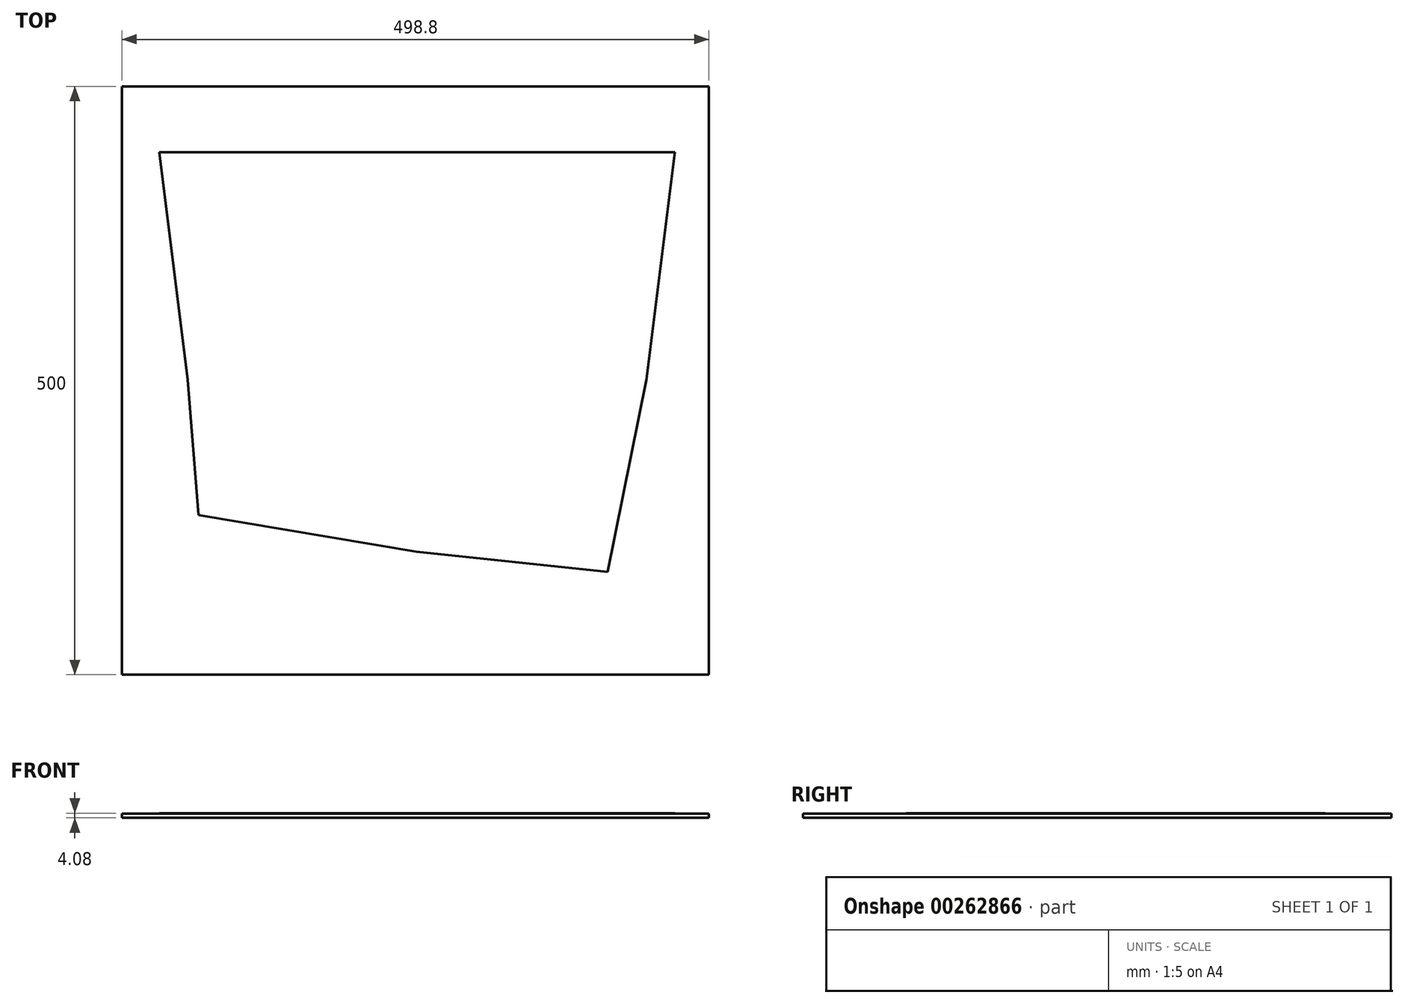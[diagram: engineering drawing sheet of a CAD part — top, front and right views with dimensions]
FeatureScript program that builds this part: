
annotation { "Feature Type Name" : "Feature", "Feature Type Description" : "" }
export const myFeature = defineFeature(function(context is Context, id is Id, definition is map)
    precondition{}
    {
        {
            var Q0;
            Q0=qCreatedBy(makeId("Top.planeOp"),FACE);
            var sketch = newSketch(context, id + "F0", { "sketchPlane" : qUnion([Q0])});
            skLineSegment(sketch, "E0.bottom", {"start": v(249.4, -250) * mm, "end": v(-249.4, -250) * mm});
            skLineSegment(sketch, "E0.top", {"start": v(249.4, 250) * mm, "end": v(-249.4, 250) * mm});
            skLineSegment(sketch, "E0.left", {"start": v(249.4, -250) * mm, "end": v(249.4, 250) * mm});
            skLineSegment(sketch, "E0.right", {"start": v(-249.4, -250) * mm, "end": v(-249.4, 250) * mm});
            skPoint(sketch, "E0.middle", {"position": v(0, 0) * mm});
            skSolve(sketch);
        }
        {
            var Q0;
            Q0=makeQuery(id+"F0.imprint","IMPRINT",FACE,{"disambiguationData":[TD([[makeQuery(id+"F0.imprint","IMPRINT",EDGE,{"derivedFrom":sQuery(id+"F0.wireOp",EDGE,"E0.bottom")}),-1.0]])]});
            extrude(context, id + "F5", {"entities" : qUnion([Q0]), "depth" : 3.58 * mm});
        }
        {
            var Q0;
            Q0=makeQuery(id+"F5.opExtrude","CAP_FACE",FACE,{"disambiguationData":[OSD([sQuery(id+"F0.wireOp",EDGE,"E0.bottom"),sQuery(id+"F0.wireOp",EDGE,"E0.top"),sQuery(id+"F0.wireOp",EDGE,"E0.left"),sQuery(id+"F0.wireOp",EDGE,"E0.right")])],"isStart":false});
            var sketch = newSketch(context, id + "F6", { "sketchPlane" : qUnion([Q0])});
            skSolve(sketch);
        }
        {
            var Q0;
            Q0=makeQuery(id+"F6.imprint","IMPRINT",FACE,{"disambiguationData":[TD([[makeQuery(id+"F6.imprint","IMPRINT",EDGE,{"derivedFrom":makeQuery(id+"F5.opExtrude","CAP_EDGE",EDGE,{"disambiguationData":[OSD([sQuery(id+"F0.wireOp",EDGE,"E0.bottom")])],"isStart":false})}),-1.0]])]});
            var sketch = newSketch(context, id + "F7", { "sketchPlane" : qUnion([Q0])});
            skLineSegment(sketch, "E1.0", {"start": v(249.4, 250) * mm, "end": v(-249.4, 250) * mm});
            skSolve(sketch);
        }
        {
            var Q0;
            Q0=makeQuery(id+"F6.imprint","IMPRINT",FACE,{"disambiguationData":[TD([[makeQuery(id+"F6.imprint","IMPRINT",EDGE,{"derivedFrom":makeQuery(id+"F5.opExtrude","CAP_EDGE",EDGE,{"disambiguationData":[OSD([sQuery(id+"F0.wireOp",EDGE,"E0.bottom")])],"isStart":false})}),-1.0]])]});
            var sketch = newSketch(context, id + "F1", { "sketchPlane" : qUnion([Q0])});
            skLineSegment(sketch, "E2", {"start": v(0, 0) * mm, "end": v(0, -288.47) * mm});
            skLineSegment(sketch, "E3", {"start": v(0, -288.47) * mm, "end": v(0, 364.66) * mm});
            skSolve(sketch);
        }
        {
            var Q0;
            Q0=makeQuery(id+"F7.imprint","IMPRINT",FACE,{"disambiguationData":[TD([[makeQuery(id+"F7.imprint","IMPRINT",EDGE,{"derivedFrom":sQuery(id+"F7.wireOp",EDGE,"E1.0")}),1.0]])]});
            var sketch = newSketch(context, id + "F2", { "sketchPlane" : qUnion([Q0])});
            skLineSegment(sketch, "E4", {"start": v(0, 0) * mm, "end": v(344.06, 0) * mm});
            skSolve(sketch);
        }
        {
            var Q0;
            Q0=makeQuery(id+"F7.imprint","IMPRINT",FACE,{"disambiguationData":[TD([[makeQuery(id+"F7.imprint","IMPRINT",EDGE,{"derivedFrom":sQuery(id+"F7.wireOp",EDGE,"E1.0")}),1.0]])]});
            var sketch = newSketch(context, id + "F8", { "sketchPlane" : qUnion([Q0])});
            skLineSegment(sketch, "E5", {"start": v(0, 0) * mm, "end": v(0, -150) * mm});
            skSolve(sketch);
        }
        {
            var Q0;
            Q0=makeQuery(id+"F8.imprint","IMPRINT",FACE,{"disambiguationData":[TD([[makeQuery(id+"F8.imprint","IMPRINT",EDGE,{"derivedFrom":makeQuery(id+"F7.imprint","IMPRINT",EDGE,{"derivedFrom":sQuery(id+"F7.wireOp",EDGE,"E1.0")})}),1.0]])]});
            var sketch = newSketch(context, id + "F9", { "sketchPlane" : qUnion([Q0])});
            skPoint(sketch, "E6", {"position": v(226.45, 198.2) * mm});
            skPoint(sketch, "E7", {"position": v(-226.46, 198.64) * mm});
            skPoint(sketch, "E8", {"position": v(-190.81, -119.49) * mm});
            skPoint(sketch, "E9", {"position": v(167.5, -166.98) * mm});
            skSolve(sketch);
        }
        {
            var Q0;
            Q0=makeQuery(id+"F8.imprint","IMPRINT",FACE,{"disambiguationData":[TD([[makeQuery(id+"F8.imprint","IMPRINT",EDGE,{"derivedFrom":makeQuery(id+"F7.imprint","IMPRINT",EDGE,{"derivedFrom":sQuery(id+"F7.wireOp",EDGE,"E1.0")})}),1.0]])]});
            var sketch = newSketch(context, id + "F3", { "sketchPlane" : qUnion([Q0])});
            skLineSegment(sketch, "E10", {"start": v(-224.62, 199.97) * mm, "end": v(0, 199.97) * mm});
            skLineSegment(sketch, "E11", {"start": v(0, 199.97) * mm, "end": v(227.13, 199.97) * mm});
            skLineSegment(sketch, "E12", {"start": v(202.14, 0) * mm, "end": v(167.97, -168.97) * mm});
            skLineSegment(sketch, "E13", {"start": v(167.97, -168.97) * mm, "end": v(0, -151.5) * mm});
            skLineSegment(sketch, "E14", {"start": v(0, -151.5) * mm, "end": v(-189.92, -119.5) * mm});
            skLineSegment(sketch, "E15", {"start": v(-189.92, -119.5) * mm, "end": v(-199.4, 0) * mm});
            skLineSegment(sketch, "E16", {"start": v(-199.4, 0) * mm, "end": v(-224.62, 199.97) * mm});
            skLineSegment(sketch, "E17", {"start": v(227.13, 199.97) * mm, "end": v(202.14, 0) * mm});
            skLineSegment(sketch, "E18", {"start": v(202.14, 0) * mm, "end": v(227.13, 199.97) * mm});
            skLineSegment(sketch, "E19", {"start": v(0, 199.97) * mm, "end": v(-224.62, 199.97) * mm});
            skLineSegment(sketch, "E20", {"start": v(-199.4, 0) * mm, "end": v(-189.92, -119.5) * mm});
            skLineSegment(sketch, "E21", {"start": v(0, -151.5) * mm, "end": v(167.97, -168.97) * mm});
            skSolve(sketch);
        }
        {
            var Q0;
            Q0=makeQuery(id+"F8.imprint","IMPRINT",FACE,{"disambiguationData":[TD([[makeQuery(id+"F8.imprint","IMPRINT",EDGE,{"derivedFrom":makeQuery(id+"F7.imprint","IMPRINT",EDGE,{"derivedFrom":sQuery(id+"F7.wireOp",EDGE,"E1.0")})}),1.0]])]});
            var sketch = newSketch(context, id + "F4", { "sketchPlane" : qUnion([Q0])});
            skLineSegment(sketch, "E22.0", {"start": v(0, 193.97) * mm, "end": v(-217.82, 193.97) * mm});
            skLineSegment(sketch, "E22.1", {"start": v(-193.43, 0.61) * mm, "end": v(-217.82, 193.97) * mm});
            skLineSegment(sketch, "E22.2", {"start": v(0, 193.97) * mm, "end": v(220.34, 193.97) * mm});
            skLineSegment(sketch, "E22.3", {"start": v(-184.3, -114.37) * mm, "end": v(-193.43, 0.61) * mm});
            skLineSegment(sketch, "E22.4", {"start": v(220.34, 193.97) * mm, "end": v(196.22, 0.97) * mm});
            skLineSegment(sketch, "E22.5", {"start": v(196.22, 0.97) * mm, "end": v(163.17, -162.43) * mm});
            skLineSegment(sketch, "E22.6", {"start": v(0.8, -145.55) * mm, "end": v(163.17, -162.43) * mm});
            skLineSegment(sketch, "E22.7", {"start": v(0.8, -145.55) * mm, "end": v(-184.3, -114.37) * mm});
            skSolve(sketch);
        }
        {
            var Q0;
            Q0=makeQuery(id+"F4.imprint","IMPRINT",FACE,{"disambiguationData":[TD([[makeQuery(id+"F4.imprint","IMPRINT",EDGE,{"derivedFrom":sQuery(id+"F4.wireOp",EDGE,"E22.0")}),1.0]])]});
            extrude(context, id + "F10", {"entities" : qUnion([Q0]), "operationType" : NewBodyOperationType.ADD, "depth" : 0.5 * mm});
        }
    });
